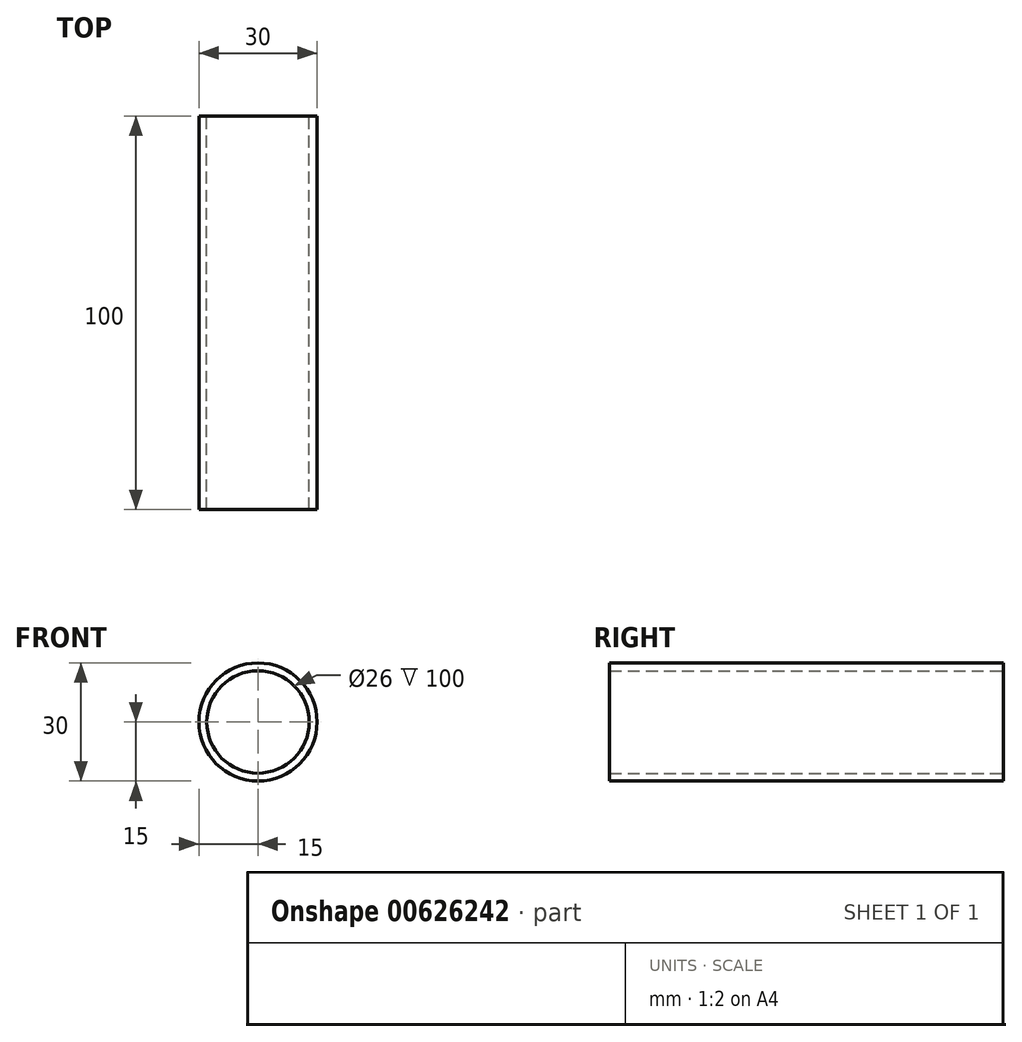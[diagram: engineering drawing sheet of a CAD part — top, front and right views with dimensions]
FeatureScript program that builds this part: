
annotation { "Feature Type Name" : "Feature", "Feature Type Description" : "" }
export const myFeature = defineFeature(function(context is Context, id is Id, definition is map)
    precondition{}
    {
        {
            var Q0;
            Q0=qCreatedBy(makeId("Front.planeOp"),FACE);
            var sketch = newSketch(context, id + "F0", { "sketchPlane" : qUnion([Q0])});
            skCircle(sketch, "E0", {"center": v(0, 0) * mm, "radius": 15 * mm});
            skCircle(sketch, "E1", {"center": v(0, 0) * mm, "radius": 13 * mm});
            skSolve(sketch);
        }
        {
            var Q0;
            Q0 = qSketchRegion(id + "F0", true);
            extrude(context, id + "F1", {"entities" : qUnion([Q0]), "endBound" : BoundingType.SYMMETRIC, "depth" : 100 * mm, "offsetDistance" : 25 * mm});
        }
    });
